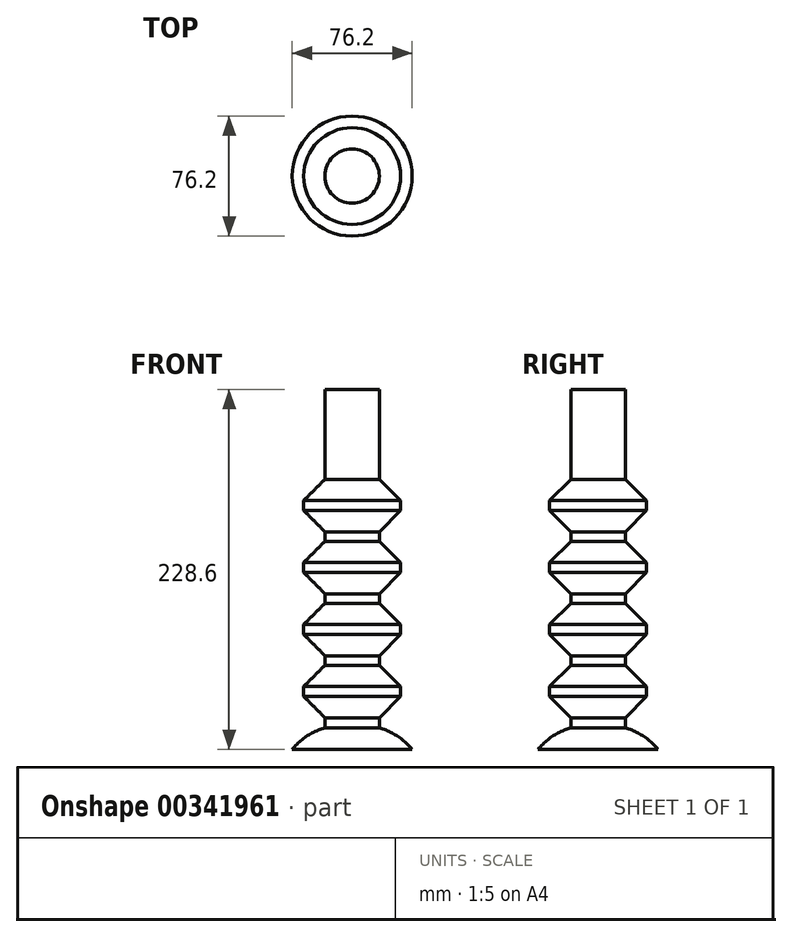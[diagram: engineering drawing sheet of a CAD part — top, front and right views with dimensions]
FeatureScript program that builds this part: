
annotation { "Feature Type Name" : "Feature", "Feature Type Description" : "" }
export const myFeature = defineFeature(function(context is Context, id is Id, definition is map)
    precondition{}
    {
        {
            var Q0;
            Q0=qCreatedBy(makeId("Front.planeOp"),FACE);
            var sketch = newSketch(context, id + "F0", { "sketchPlane" : qUnion([Q0])});
            skLineSegment(sketch, "E0", {"start": v(0, 123.39) * mm, "end": v(0, -105.21) * mm});
            skLineSegment(sketch, "E1", {"start": v(0, -105.21) * mm, "end": v(-38.1, -105.21) * mm});
            skArc(sketch, "E2", {"start": v(-17.29, -91.38) * mm, "mid": v(-28.72, -96.75) * mm, "end": v(-38.1, -105.21) * mm});
            skLineSegment(sketch, "E3", {"start": v(-17.29, -91.38) * mm, "end": v(-17.29, -85.03) * mm});
            skLineSegment(sketch, "E4", {"start": v(-17.29, -85.03) * mm, "end": v(-30.76, -71.56) * mm});
            skLineSegment(sketch, "E5", {"start": v(-30.76, -71.56) * mm, "end": v(-30.76, -65.21) * mm});
            skLineSegment(sketch, "E6", {"start": v(-30.76, -65.21) * mm, "end": v(-17.29, -51.74) * mm});
            skLineSegment(sketch, "E7", {"start": v(-17.29, -51.74) * mm, "end": v(-17.29, -45.4) * mm});
            skLineSegment(sketch, "E8.0.1.0", {"start": v(-17.29, -12.37) * mm, "end": v(-17.29, -6.02) * mm});
            skLineSegment(sketch, "E8.0.1.1", {"start": v(-30.76, -25.84) * mm, "end": v(-17.29, -12.37) * mm});
            skLineSegment(sketch, "E8.0.1.2", {"start": v(-30.76, -32.2) * mm, "end": v(-30.76, -25.84) * mm});
            skLineSegment(sketch, "E8.0.1.3", {"start": v(-17.29, -45.66) * mm, "end": v(-30.76, -32.2) * mm});
            skLineSegment(sketch, "E8.0.2.0", {"start": v(-17.29, 27) * mm, "end": v(-17.29, 33.35) * mm});
            skLineSegment(sketch, "E8.0.2.1", {"start": v(-30.76, 13.53) * mm, "end": v(-17.29, 27) * mm});
            skLineSegment(sketch, "E8.0.2.2", {"start": v(-30.76, 7.18) * mm, "end": v(-30.76, 13.53) * mm});
            skLineSegment(sketch, "E8.0.2.3", {"start": v(-17.29, -6.3) * mm, "end": v(-30.76, 7.18) * mm});
            skLineSegment(sketch, "E8.0.3.0", {"start": v(-17.29, 66.37) * mm, "end": v(-17.29, 72.72) * mm});
            skLineSegment(sketch, "E8.0.3.1", {"start": v(-30.76, 52.9) * mm, "end": v(-17.29, 66.37) * mm});
            skLineSegment(sketch, "E8.0.3.2", {"start": v(-30.76, 46.55) * mm, "end": v(-30.76, 52.9) * mm});
            skLineSegment(sketch, "E8.0.3.3", {"start": v(-17.29, 33.08) * mm, "end": v(-30.76, 46.55) * mm});
            skLineSegment(sketch, "E8.direction1", {"start": v(-17.29, -51.74) * mm, "end": v(8.11, -51.74) * mm, "construction": true});
            skLineSegment(sketch, "E8.direction2", {"start": v(-17.29, -51.74) * mm, "end": v(-17.29, -12.37) * mm, "construction": true});
            skLineSegment(sketch, "E9", {"start": v(-17.29, 72.72) * mm, "end": v(-17.29, 123.39) * mm});
            skLineSegment(sketch, "E10", {"start": v(-17.29, 123.39) * mm, "end": v(0, 123.39) * mm});
            skSolve(sketch);
        }
        {
            var Q0;
            Q0 = qSketchRegion(id + "F0", true);
            var Q1;
            Q1=sQuery(id+"F0.wireOp",EDGE,"E0");
            revolve(context, id + "F1", {"entities" : qUnion([Q0]), "axis" : qUnion([Q1]), "revolveType" : RevolveType.FULL, "oppositeDirection" : true});
        }
    });
